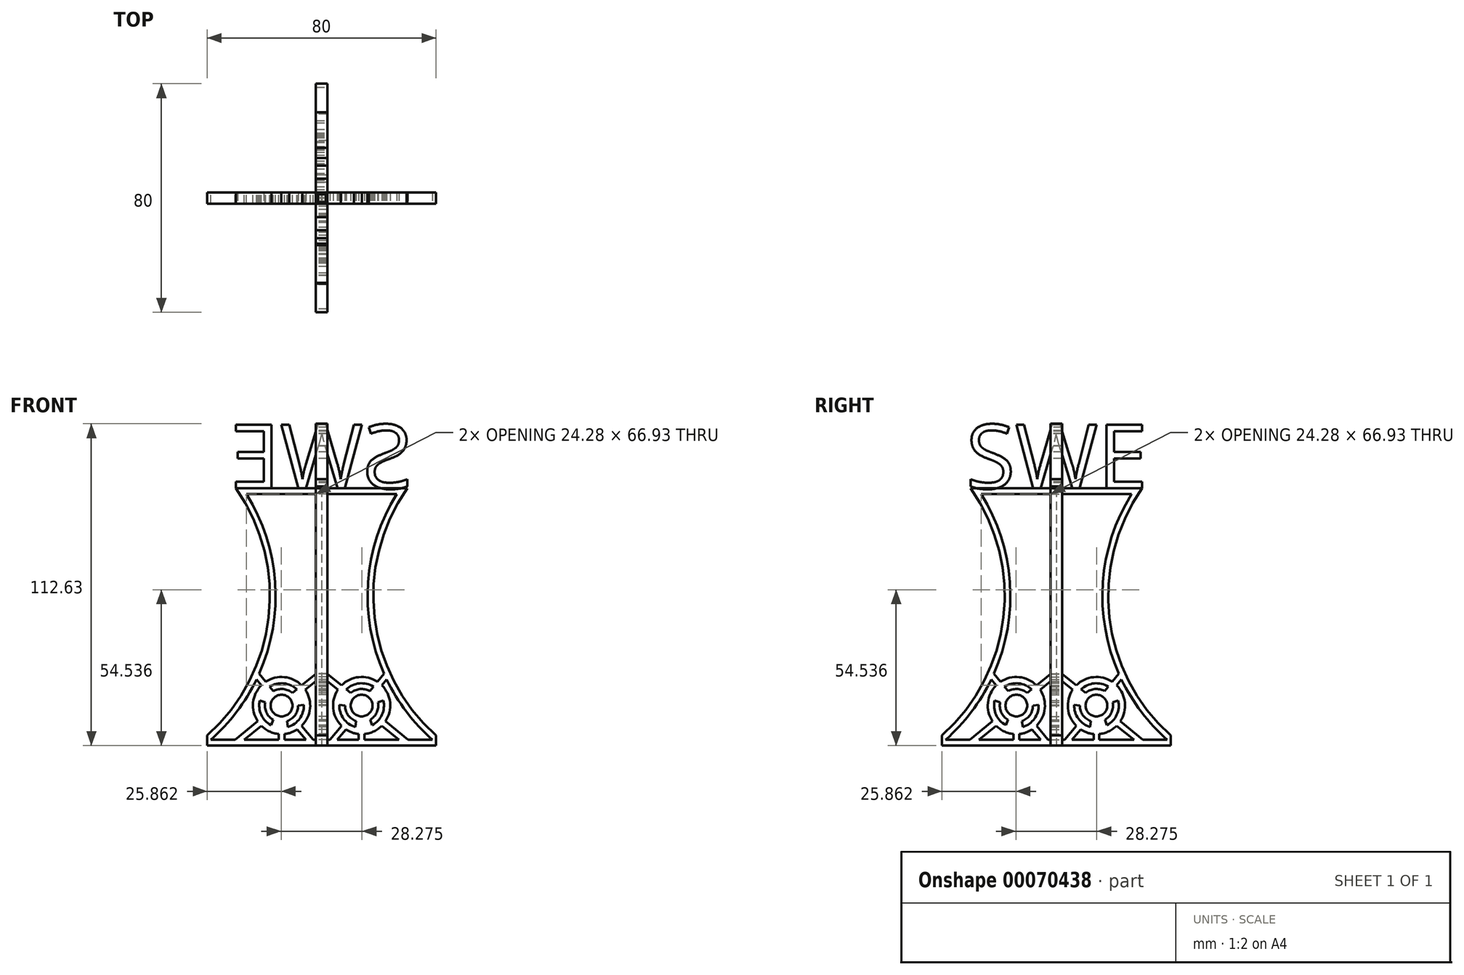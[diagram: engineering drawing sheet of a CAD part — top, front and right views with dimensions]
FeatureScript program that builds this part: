
annotation { "Feature Type Name" : "Feature", "Feature Type Description" : "" }
export const myFeature = defineFeature(function(context is Context, id is Id, definition is map)
    precondition{}
    {
        {
            var Q0;
            Q0=qCreatedBy(makeId("Right.planeOp"),FACE);
            var sketch = newSketch(context, id + "F0", { "sketchPlane" : qUnion([Q0])});
            skLineSegment(sketch, "E0", {"start": v(-30, 90) * mm, "end": v(0, 90) * mm});
            skLineSegment(sketch, "E1", {"start": v(0, 90) * mm, "end": v(0, 0) * mm});
            skLineSegment(sketch, "E2", {"start": v(0, 0) * mm, "end": v(-40, 0) * mm});
            skLineSegment(sketch, "E3", {"start": v(-40, 0) * mm, "end": v(-40, 3.59) * mm});
            skArc(sketch, "E4", {"start": v(-40, 3.59) * mm, "mid": v(-18.52, 44.89) * mm, "end": v(-30, 90) * mm});
            skArc(sketch, "E5", {"start": v(-6.93, 6.93) * mm, "mid": v(-4.05, 13) * mm, "end": v(-5.66, 19.52) * mm});
            skArc(sketch, "E6.0", {"start": v(-38.77, 2) * mm, "mid": v(-29.72, 11.78) * mm, "end": v(-22.77, 23.15) * mm});
            skLineSegment(sketch, "E6.1", {"start": v(-2, 2) * mm, "end": v(-13, 2) * mm});
            skLineSegment(sketch, "E6.2", {"start": v(-2, 88) * mm, "end": v(-2, 25.1) * mm});
            skLineSegment(sketch, "E6.3", {"start": v(-26.28, 88) * mm, "end": v(-2, 88) * mm});
            skLineSegment(sketch, "E7", {"start": v(-30.26, 2) * mm, "end": v(-22.34, 8.48) * mm});
            skLineSegment(sketch, "E8", {"start": v(-27.1, 2) * mm, "end": v(-21.07, 6.93) * mm});
            skLineSegment(sketch, "E9", {"start": v(-2, 0.9) * mm, "end": v(-6.93, 6.93) * mm});
            skLineSegment(sketch, "E10", {"start": v(-5.48, 2) * mm, "end": v(-8.48, 5.66) * mm});
            skLineSegment(sketch, "E11.trimOffspring", {"start": v(-6.93, 21.07) * mm, "end": v(-2, 25.1) * mm});
            skLineSegment(sketch, "E12.trimOffspring", {"start": v(-5.66, 19.52) * mm, "end": v(-2, 22.52) * mm});
            skLineSegment(sketch, "E13.trimOffspring", {"start": v(-19.52, 22.34) * mm, "end": v(-21.84, 25.17) * mm});
            skLineSegment(sketch, "E14.trimOffspring", {"start": v(-21.07, 21.07) * mm, "end": v(-22.77, 23.15) * mm});
            skArc(sketch, "E15.trimOffspring", {"start": v(-21.07, 6.93) * mm, "mid": v(-18.28, 4.96) * mm, "end": v(-15, 4.05) * mm});
            skArc(sketch, "E16.trimOffspring", {"start": v(-21.07, 21.07) * mm, "mid": v(-23.95, 15) * mm, "end": v(-22.34, 8.48) * mm});
            skArc(sketch, "E17.trimOffspring", {"start": v(-21.84, 25.17) * mm, "mid": v(-16.26, 57.14) * mm, "end": v(-26.28, 88) * mm});
            skArc(sketch, "E18.trimOffspring", {"start": v(-6.93, 21.07) * mm, "mid": v(-13, 23.95) * mm, "end": v(-19.52, 22.34) * mm});
            skLineSegment(sketch, "E19.trimOffspring", {"start": v(-2, 22.52) * mm, "end": v(-2, 2) * mm});
            skCircle(sketch, "E20", {"center": v(-14, 14) * mm, "radius": 7.8 * mm, "construction": true});
            skCircle(sketch, "E21", {"center": v(-14, 14) * mm, "radius": 5.8 * mm, "construction": true});
            skLineSegment(sketch, "E22", {"start": v(-19.52, 22.34) * mm, "end": v(-6.93, 6.93) * mm, "construction": true});
            skLineSegment(sketch, "E23", {"start": v(-21.07, 21.07) * mm, "end": v(-8.48, 5.66) * mm, "construction": true});
            skLineSegment(sketch, "E24", {"start": v(-6.93, 21.07) * mm, "end": v(-22.34, 8.48) * mm, "construction": true});
            skLineSegment(sketch, "E25", {"start": v(-5.66, 19.52) * mm, "end": v(-21.07, 6.93) * mm, "construction": true});
            skArc(sketch, "E26", {"start": v(-8.64, 19.67) * mm, "mid": v(-13.22, 21.76) * mm, "end": v(-18.12, 20.62) * mm});
            skArc(sketch, "E27", {"start": v(-10.2, 18.39) * mm, "mid": v(-13.42, 19.77) * mm, "end": v(-16.84, 19.06) * mm});
            skLineSegment(sketch, "E28", {"start": v(-18.12, 20.62) * mm, "end": v(-16.84, 19.06) * mm});
            skLineSegment(sketch, "E29", {"start": v(-8.64, 19.67) * mm, "end": v(-10.2, 18.39) * mm});
            skArc(sketch, "E30.1.0", {"start": v(-21.59, 15.8) * mm, "mid": v(-21.11, 10.8) * mm, "end": v(-17.67, 7.12) * mm});
            skLineSegment(sketch, "E30.1.1", {"start": v(-17.67, 7.12) * mm, "end": v(-16.96, 9.01) * mm});
            skArc(sketch, "E30.1.2", {"start": v(-19.7, 15.09) * mm, "mid": v(-19.29, 11.62) * mm, "end": v(-16.96, 9.01) * mm});
            skLineSegment(sketch, "E30.1.3", {"start": v(-21.59, 15.8) * mm, "end": v(-19.7, 15.09) * mm});
            skArc(sketch, "E30.2.0", {"start": v(-11.77, 6.53) * mm, "mid": v(-7.67, 9.44) * mm, "end": v(-6.2, 14.26) * mm});
            skLineSegment(sketch, "E30.2.1", {"start": v(-6.2, 14.26) * mm, "end": v(-8.2, 13.93) * mm});
            skArc(sketch, "E30.2.2", {"start": v(-12.1, 8.52) * mm, "mid": v(-9.3, 10.61) * mm, "end": v(-8.2, 13.93) * mm});
            skLineSegment(sketch, "E30.2.3", {"start": v(-11.77, 6.53) * mm, "end": v(-12.1, 8.52) * mm});
            skCircle(sketch, "E31", {"center": v(-14, 14) * mm, "radius": 3.8 * mm});
            skLineSegment(sketch, "E32", {"start": v(-15, 4.05) * mm, "end": v(-15, 2) * mm});
            skLineSegment(sketch, "E33", {"start": v(-13, 4.05) * mm, "end": v(-13, 2) * mm});
            skPoint(sketch, "E33.startSnap0", {"position": v(-15, 4.05) * mm});
            skArc(sketch, "E34.trimOffspring", {"start": v(-13, 4.05) * mm, "mid": v(-10.64, 4.58) * mm, "end": v(-8.48, 5.66) * mm});
            skLineSegment(sketch, "E35.trimOffspring", {"start": v(-15, 2) * mm, "end": v(-38.77, 2) * mm});
            skSolve(sketch);
        }
        {
            var Q0;
            Q0=qSketchRegion(id+"F0",true);
            extrude(context, id + "F1", {"entities" : qUnion([Q0]), "depth" : 2 * mm, "hasSecondDirection" : true, "secondDirectionOppositeDirection" : true, "secondDirectionDepth" : 2 * mm});
        }
        {
            var Q0;
            Q0=qCreatedBy(makeId("Right.planeOp"),FACE);
            var sketch = newSketch(context, id + "F2", { "sketchPlane" : qUnion([Q0])});
            skLineSegment(sketch, "E36", {"start": v(0, 81) * mm, "end": v(0, -28.5) * mm, "construction": true});
            skSolve(sketch);
        }
        {
            var Q0;
            Q0=makeQuery(id+"F1.opExtrude","SWEPT_BODY",BODY,{"disambiguationData":[OSD([sQuery(id+"F0.wireOp",EDGE,"E0"),sQuery(id+"F0.wireOp",EDGE,"E1"),sQuery(id+"F0.wireOp",EDGE,"N8EfN9Iy-VFxy-i62X-S3Tn-et34u0hB6ofw"),sQuery(id+"F0.wireOp",EDGE,"ofOerVMI-8AtS-AqWo-Xm8z-ZVAlB3EUovam"),sQuery(id+"F0.wireOp",EDGE,"ba3e6201-bb00-4176-be12-0bcf97df4df2"),sQuery(id+"F0.wireOp",EDGE,"k6Ju8hmT-RXya-gFIe-6RDm-fDKX84Fwp2G4"),sQuery(id+"F0.wireOp",EDGE,"dTDJtstR-zKxY-rc8w-sIGn-4ASnDpw26A23"),sQuery(id+"F0.wireOp",EDGE,"Cvr0LfUC-tO0D-IxcI-B5Ti-WW2sAGeSHFF8"),sQuery(id+"F0.wireOp",EDGE,"DwRJblST-1CEV-pcTT-NFQT-YytcCcE5cTGx"),sQuery(id+"F0.wireOp",EDGE,"973229ff-babc-457a-ac66-6eeaf75bea45")])]});
            var Q1;
            Q1=sQuery(id+"F2.wireOp",EDGE,"E36");
            circularPattern(context, id + "F3", {"entities" : qUnion([Q0]), "axis" : qUnion([Q1]), "angle" : 90 * degree, "instanceCount" : round(4)});
        }
        {
            var Q0;
            Q0=qCreatedBy(makeId("Right.planeOp"),FACE);
            var sketch = newSketch(context, id + "F4", { "sketchPlane" : qUnion([Q0])});
            skText(sketch, "E37", { "text": "SWE", "fontName": "OpenSans-Regular.ttf"});
            const initialGuessF4  = {"E37": [-0.0316, 0.09, 1, 0, 0.0225]};
            skSetInitialGuess(sketch, initialGuessF4);
            skSolve(sketch);
        }
        {
            var Q0;
            Q0 = qSketchRegion(id + "F4", true);
            extrude(context, id + "F5", {"entities" : qUnion([Q0]), "depth" : 2 * mm, "hasSecondDirection" : true, "secondDirectionOppositeDirection" : true, "secondDirectionDepth" : 2 * mm});
        }
        {
            var Q0;
            Q0=qCreatedBy(makeId("Right.planeOp"),FACE);
            var sketch = newSketch(context, id + "F6", { "sketchPlane" : qUnion([Q0])});
            skLineSegment(sketch, "E38", {"start": v(0, 67.06) * mm, "end": v(0, 97.37) * mm, "construction": true});
            skSolve(sketch);
        }
        {
            var Q0;
            Q0=makeQuery(id+"F5.opExtrude","SWEPT_BODY",BODY,{"disambiguationData":[OSD([sQuery(id+"F4.wireOp",EDGE,"E37.sketch_text.stroke-45"),sQuery(id+"F4.wireOp",EDGE,"E37.sketch_text.stroke-46"),sQuery(id+"F4.wireOp",EDGE,"E37.sketch_text.stroke-47"),sQuery(id+"F4.wireOp",EDGE,"E37.sketch_text.stroke-48"),sQuery(id+"F4.wireOp",EDGE,"E37.sketch_text.stroke-49"),sQuery(id+"F4.wireOp",EDGE,"E37.sketch_text.stroke-50"),sQuery(id+"F4.wireOp",EDGE,"E37.sketch_text.stroke-51"),sQuery(id+"F4.wireOp",EDGE,"E37.sketch_text.stroke-52"),sQuery(id+"F4.wireOp",EDGE,"E37.sketch_text.stroke-53"),sQuery(id+"F4.wireOp",EDGE,"E37.sketch_text.stroke-54"),sQuery(id+"F4.wireOp",EDGE,"E37.sketch_text.stroke-55"),sQuery(id+"F4.wireOp",EDGE,"E37.sketch_text.stroke-56")])]});
            var Q1;
            Q1=makeQuery(id+"F5.opExtrude","SWEPT_BODY",BODY,{"disambiguationData":[OSD([sQuery(id+"F4.wireOp",EDGE,"E37.sketch_text.stroke-25"),sQuery(id+"F4.wireOp",EDGE,"E37.sketch_text.stroke-26"),sQuery(id+"F4.wireOp",EDGE,"E37.sketch_text.stroke-27"),sQuery(id+"F4.wireOp",EDGE,"E37.sketch_text.stroke-28"),sQuery(id+"F4.wireOp",EDGE,"E37.sketch_text.stroke-29"),sQuery(id+"F4.wireOp",EDGE,"E37.sketch_text.stroke-30"),sQuery(id+"F4.wireOp",EDGE,"E37.sketch_text.stroke-31"),sQuery(id+"F4.wireOp",EDGE,"E37.sketch_text.stroke-32"),sQuery(id+"F4.wireOp",EDGE,"E37.sketch_text.stroke-33"),sQuery(id+"F4.wireOp",EDGE,"E37.sketch_text.stroke-34"),sQuery(id+"F4.wireOp",EDGE,"E37.sketch_text.stroke-35"),sQuery(id+"F4.wireOp",EDGE,"E37.sketch_text.stroke-36"),sQuery(id+"F4.wireOp",EDGE,"E37.sketch_text.stroke-37"),sQuery(id+"F4.wireOp",EDGE,"E37.sketch_text.stroke-38"),sQuery(id+"F4.wireOp",EDGE,"E37.sketch_text.stroke-39"),sQuery(id+"F4.wireOp",EDGE,"E37.sketch_text.stroke-40"),sQuery(id+"F4.wireOp",EDGE,"E37.sketch_text.stroke-41"),sQuery(id+"F4.wireOp",EDGE,"E37.sketch_text.stroke-42"),sQuery(id+"F4.wireOp",EDGE,"E37.sketch_text.stroke-43"),sQuery(id+"F4.wireOp",EDGE,"E37.sketch_text.stroke-44")])]});
            var Q2;
            Q2=makeQuery(id+"F5.opExtrude","SWEPT_BODY",BODY,{"disambiguationData":[OSD([sQuery(id+"F4.wireOp",EDGE,"E37.sketch_text.stroke-0"),sQuery(id+"F4.wireOp",EDGE,"E37.sketch_text.stroke-1"),sQuery(id+"F4.wireOp",EDGE,"E37.sketch_text.stroke-2"),sQuery(id+"F4.wireOp",EDGE,"E37.sketch_text.stroke-3"),sQuery(id+"F4.wireOp",EDGE,"E37.sketch_text.stroke-4"),sQuery(id+"F4.wireOp",EDGE,"E37.sketch_text.stroke-5"),sQuery(id+"F4.wireOp",EDGE,"E37.sketch_text.stroke-6"),sQuery(id+"F4.wireOp",EDGE,"E37.sketch_text.stroke-7"),sQuery(id+"F4.wireOp",EDGE,"E37.sketch_text.stroke-8"),sQuery(id+"F4.wireOp",EDGE,"E37.sketch_text.stroke-9"),sQuery(id+"F4.wireOp",EDGE,"E37.sketch_text.stroke-10"),sQuery(id+"F4.wireOp",EDGE,"E37.sketch_text.stroke-11"),sQuery(id+"F4.wireOp",EDGE,"E37.sketch_text.stroke-12"),sQuery(id+"F4.wireOp",EDGE,"E37.sketch_text.stroke-13"),sQuery(id+"F4.wireOp",EDGE,"E37.sketch_text.stroke-14"),sQuery(id+"F4.wireOp",EDGE,"E37.sketch_text.stroke-15"),sQuery(id+"F4.wireOp",EDGE,"E37.sketch_text.stroke-16"),sQuery(id+"F4.wireOp",EDGE,"E37.sketch_text.stroke-17"),sQuery(id+"F4.wireOp",EDGE,"E37.sketch_text.stroke-18"),sQuery(id+"F4.wireOp",EDGE,"E37.sketch_text.stroke-19"),sQuery(id+"F4.wireOp",EDGE,"E37.sketch_text.stroke-20"),sQuery(id+"F4.wireOp",EDGE,"E37.sketch_text.stroke-21"),sQuery(id+"F4.wireOp",EDGE,"E37.sketch_text.stroke-22"),sQuery(id+"F4.wireOp",EDGE,"E37.sketch_text.stroke-23"),sQuery(id+"F4.wireOp",EDGE,"E37.sketch_text.stroke-24")])]});
            var Q3;
            Q3=sQuery(id+"F6.wireOp",EDGE,"E38");
            circularPattern(context, id + "F7", {"entities" : qUnion([Q0, Q1, Q2]), "axis" : qUnion([Q3]), "angle" : 90 * degree, "instanceCount" : 2});
        }
    });
